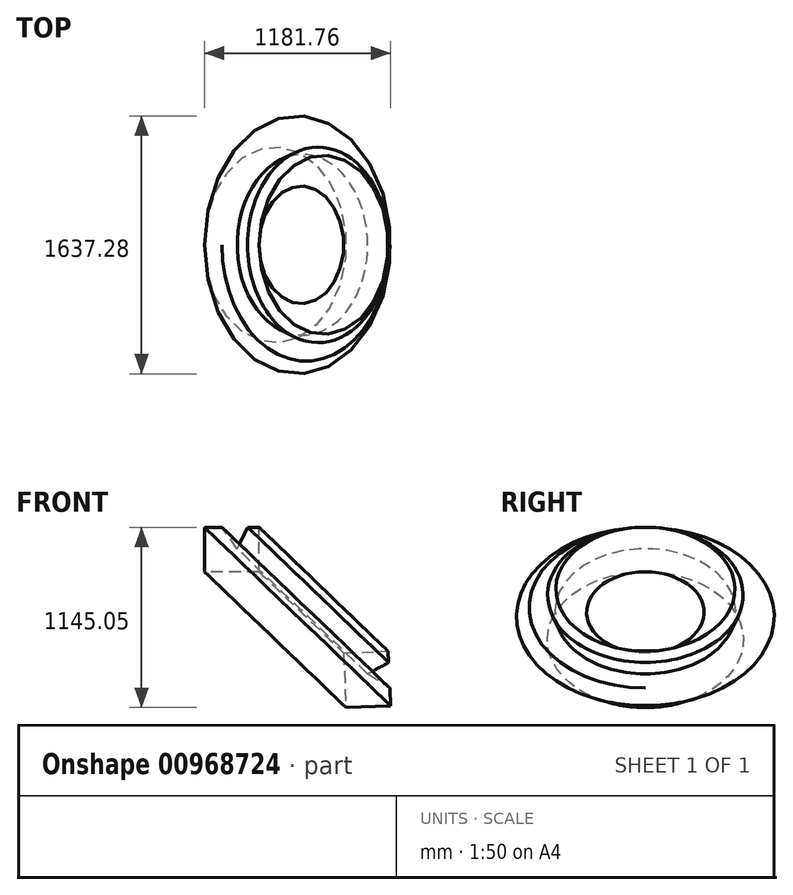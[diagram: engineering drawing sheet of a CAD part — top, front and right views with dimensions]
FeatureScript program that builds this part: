
annotation { "Feature Type Name" : "Feature", "Feature Type Description" : "" }
export const myFeature = defineFeature(function(context is Context, id is Id, definition is map)
    precondition{}
    {
        {
            var Q0;
            Q0=qCreatedBy(makeId("Front.planeOp"),FACE);
            var sketch = newSketch(context, id + "F0", { "sketchPlane" : qUnion([Q0])});
            skLineSegment(sketch, "E0", {"start": v(0, 0) * mm, "end": v(0, 304.8) * mm, "construction": true});
            skLineSegment(sketch, "E1.bottom", {"start": v(492.46, -398.8) * mm, "end": v(838.94, -398.8) * mm});
            skLineSegment(sketch, "E1.top", {"start": v(492.46, -681.46) * mm, "end": v(838.94, -681.46) * mm});
            skLineSegment(sketch, "E1.left", {"start": v(492.46, -398.8) * mm, "end": v(492.46, -681.46) * mm});
            skLineSegment(sketch, "E1.right", {"start": v(838.94, -398.8) * mm, "end": v(838.94, -681.46) * mm});
            skLineSegment(sketch, "E2", {"start": v(980.21, -1072.95) * mm, "end": v(1484.98, -546.55) * mm, "construction": true});
            skSolve(sketch);
        }
        {
            var Q0;
            Q0=makeQuery(id+"F0.imprint","IMPRINT",FACE,{"disambiguationData":[TD([[makeQuery(id+"F0.imprint","IMPRINT",EDGE,{"derivedFrom":sQuery(id+"F0.wireOp",EDGE,"E1.bottom")}),-1.0]])]});
            var Q1;
            Q1=sQuery(id+"F0.wireOp",EDGE,"E2");
            revolve(context, id + "F1", {"surfaceOperationType" : NewSurfaceOperationType.NEW, "entities" : qUnion([Q0]), "axis" : qUnion([Q1]), "revolveType" : RevolveType.FULL});
        }
        {
            var Q0;
            Q0=qCreatedBy(makeId("Front.planeOp"),FACE);
            var sketch = newSketch(context, id + "F2", { "sketchPlane" : qUnion([Q0])});
            skLineSegment(sketch, "E3", {"start": v(527.88, -291.43) * mm, "end": v(700.78, -535.05) * mm});
            skLineSegment(sketch, "E4", {"start": v(700.78, -535.05) * mm, "end": v(834.37, -260) * mm});
            skLineSegment(sketch, "E5", {"start": v(834.37, -260) * mm, "end": v(527.88, -291.43) * mm});
            skSolve(sketch);
        }
        {
            var Q0;
            Q0 = qSketchRegion(id + "F2", true);
            var Q1;
            Q1=sQuery(id+"F0.wireOp",EDGE,"E2");
            revolve(context, id + "F3", {"operationType" : NewBodyOperationType.REMOVE, "surfaceOperationType" : NewSurfaceOperationType.NEW, "entities" : qUnion([Q0]), "axis" : qUnion([Q1]), "revolveType" : RevolveType.FULL, "oppositeDirection" : true});
        }
    });
